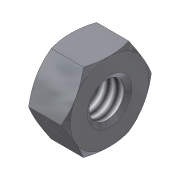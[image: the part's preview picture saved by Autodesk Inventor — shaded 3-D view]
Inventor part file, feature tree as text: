
AUTODESK INVENTOR PART (.ipt)
format: ipt  version: 2014 (Build 180170000, 170)  size: 147,456 bytes
history: native  units: mm (DEFAULTED — no unit token found)
features: sketch x3, chamfer x1, hole x1
ambient origin geometry x8: Origin, YZ Plane, XZ Plane, XY Plane, X Axis, Y Axis, Z Axis, Center Point
bodies: Solid1 (feature_tree), Body (feature_tree)
feature tree (5):
  chamfer  "Chamfer1"  Angle=30.0deg  [1 undecoded]
  hole  "Thread"  [1 undecoded]
  sketch  "Sketch1"  dims[d0=12.83161mm]
  sketch  "Sketch2"  dims[d1=5.5626mm]
  sketch  "Sketch3"  dims[d2=0.0mm d3=30.0deg d4=30.0deg d5=11.1125mm d6=11.1125mm d7=90.0deg d25=4.9784mm d26=6.0mm d27=4.0mm d28=2.0mm d29=14.3117mm d30=8.0mm d31=20.594885mm d8=0.687408mm d9=30.0deg d10=0.687408mm d11=30.0deg d13=0.0mm d14=0.0mm d39=0.0mm d40=0.687408mm d41=0.687408mm]
note: 2 required parameter values undecoded (feature->parameter linkage not recoverable at this tier; creation-order binding heuristic only, values carry confidence <= 0.55)
